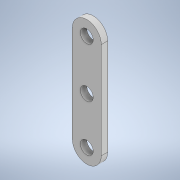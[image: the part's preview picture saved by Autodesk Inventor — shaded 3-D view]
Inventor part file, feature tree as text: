
AUTODESK INVENTOR PART (.ipt)
format: ipt  version: 2021 (Build 250183000, 183)  size: 113,664 bytes
history: native  units: mm
features: extrude x1, sketch x1
ambient origin geometry x8: Origin, YZ Plane, XZ Plane, XY Plane, X Axis, Y Axis, Z Axis, Center Point
bodies: Solid1 (feature_tree)
feature tree (2):
  extrude  "Extrusion1"  Depth=4.0mm
  sketch  "Sketch1"  dims[d0=18.0mm d1=78.0mm d2=8.0mm d3=9.0mm d4=8.0mm d5=8.0mm d6=4.0mm d7=0.0mm]
